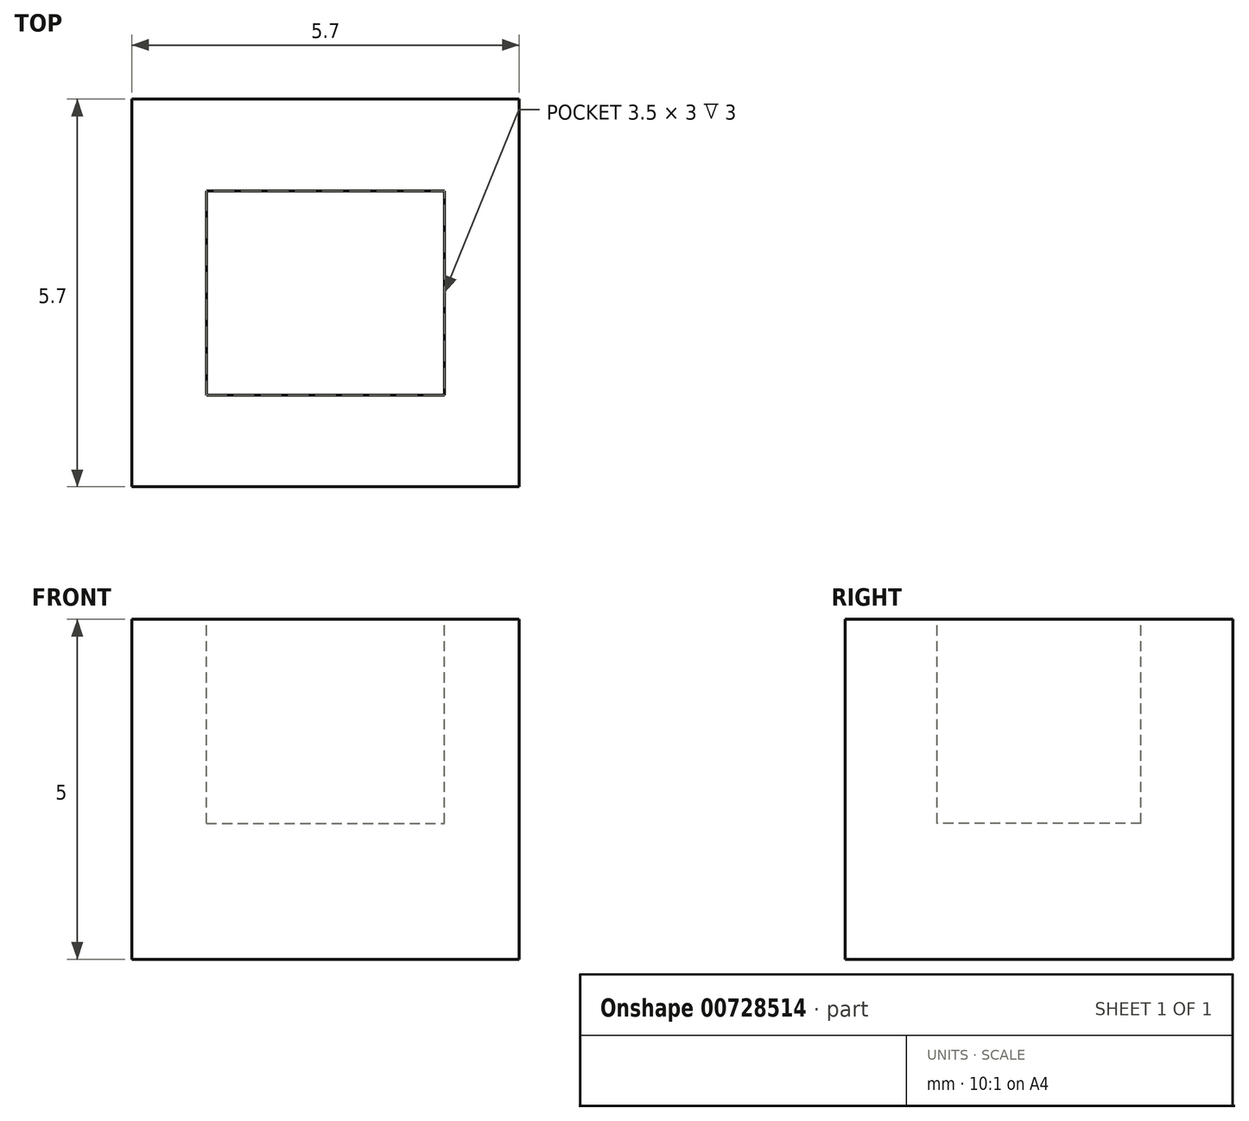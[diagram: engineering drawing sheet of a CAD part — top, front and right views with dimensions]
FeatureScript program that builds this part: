
annotation { "Feature Type Name" : "Feature", "Feature Type Description" : "" }
export const myFeature = defineFeature(function(context is Context, id is Id, definition is map)
    precondition{}
    {
        {
            var Q0;
            Q0=qCreatedBy(makeId("Top.planeOp"),FACE);
            var sketch = newSketch(context, id + "F0", { "sketchPlane" : qUnion([Q0])});
            skLineSegment(sketch, "E0.bottom", {"start": v(0, 0) * mm, "end": v(5.7, 0) * mm});
            skLineSegment(sketch, "E0.top", {"start": v(0, -5.7) * mm, "end": v(5.7, -5.7) * mm});
            skLineSegment(sketch, "E0.left", {"start": v(0, 0) * mm, "end": v(0, -5.7) * mm});
            skLineSegment(sketch, "E0.right", {"start": v(5.7, 0) * mm, "end": v(5.7, -5.7) * mm});
            skSolve(sketch);
        }
        {
            var Q0;
            Q0=makeQuery(id+"F0.imprint","IMPRINT",FACE,{"disambiguationData":[TD([[makeQuery(id+"F0.imprint","IMPRINT",EDGE,{"derivedFrom":sQuery(id+"F0.wireOp",EDGE,"E0.bottom")}),-1.0]])]});
            extrude(context, id + "F1", {"entities" : qUnion([Q0]), "depth" : 5 * mm, "offsetDistance" : 25 * mm});
        }
        {
            var Q0;
            Q0=makeQuery(id+"F1.opExtrude","CAP_FACE",FACE,{"disambiguationData":[OSD([sQuery(id+"F0.wireOp",EDGE,"E0.bottom"),sQuery(id+"F0.wireOp",EDGE,"E0.top"),sQuery(id+"F0.wireOp",EDGE,"E0.left"),sQuery(id+"F0.wireOp",EDGE,"E0.right")])],"isStart":false});
            var sketch = newSketch(context, id + "F2", { "sketchPlane" : qUnion([Q0])});
            skLineSegment(sketch, "E1.bottom", {"start": v(1.1, -1.35) * mm, "end": v(4.6, -1.35) * mm});
            skLineSegment(sketch, "E1.top", {"start": v(1.1, -4.35) * mm, "end": v(4.6, -4.35) * mm});
            skLineSegment(sketch, "E1.left", {"start": v(1.1, -1.35) * mm, "end": v(1.1, -4.35) * mm});
            skLineSegment(sketch, "E1.right", {"start": v(4.6, -1.35) * mm, "end": v(4.6, -4.35) * mm});
            skLineSegment(sketch, "E2", {"start": v(2.85, -5.7) * mm, "end": v(2.85, 0) * mm, "construction": true});
            skLineSegment(sketch, "E3", {"start": v(0, -2.85) * mm, "end": v(5.7, -2.85) * mm, "construction": true});
            skSolve(sketch);
        }
        {
            var Q0;
            Q0 = qSketchRegion(id + "F2", true);
            extrude(context, id + "F3", {"entities" : qUnion([Q0]), "operationType" : NewBodyOperationType.REMOVE, "oppositeDirection" : true, "depth" : 3 * mm, "offsetDistance" : 25 * mm});
        }
    });
